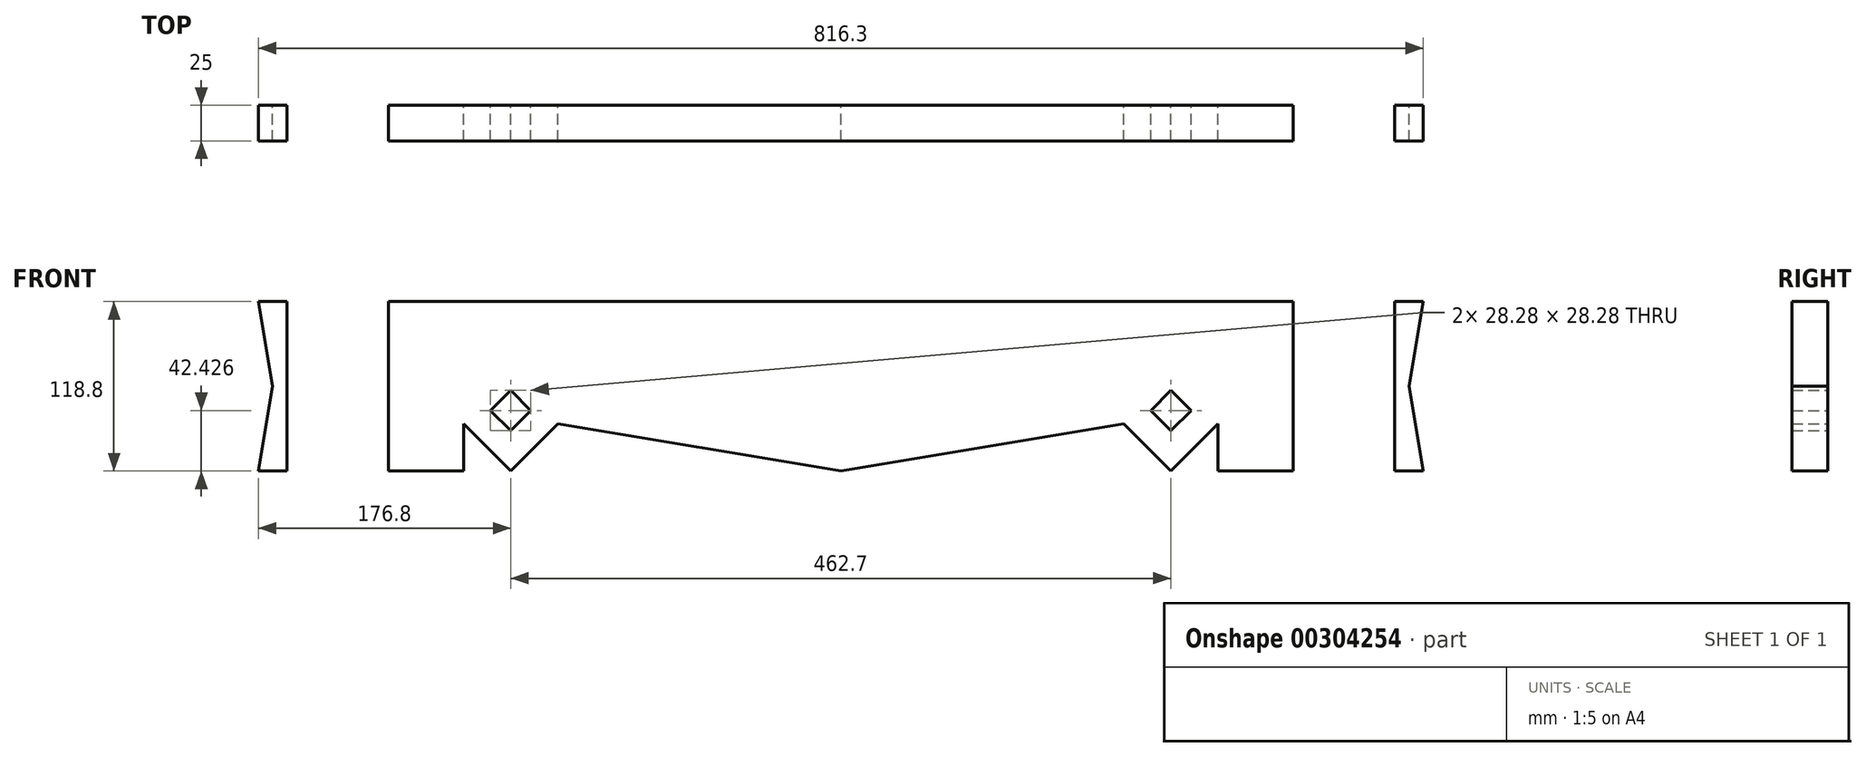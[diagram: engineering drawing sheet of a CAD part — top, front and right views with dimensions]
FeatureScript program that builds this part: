
annotation { "Feature Type Name" : "Feature", "Feature Type Description" : "" }
export const myFeature = defineFeature(function(context is Context, id is Id, definition is map)
    precondition{}
    {
        {
            var Q0;
            Q0=qCreatedBy(makeId("Front.planeOp"),FACE);
            var sketch = newSketch(context, id + "F0", { "sketchPlane" : qUnion([Q0])});
            skLineSegment(sketch, "E0.bottom", {"start": v(408.15, -59.4) * mm, "end": v(-408.15, -59.4) * mm});
            skLineSegment(sketch, "E0.top", {"start": v(408.15, 59.4) * mm, "end": v(-408.15, 59.4) * mm});
            skLineSegment(sketch, "E0.left", {"start": v(408.15, -59.4) * mm, "end": v(408.15, 59.4) * mm});
            skLineSegment(sketch, "E0.right", {"start": v(-408.15, -59.4) * mm, "end": v(-408.15, 59.4) * mm});
            skPoint(sketch, "E0.middle", {"position": v(0, 0) * mm});
            skLineSegment(sketch, "E1", {"start": v(-408.15, 0) * mm, "end": v(408.15, 0) * mm, "construction": true});
            skPoint(sketch, "E2", {"position": v(-398.15, 0) * mm});
            skLineSegment(sketch, "E3", {"start": v(-408.15, 59.4) * mm, "end": v(-398.15, 0) * mm});
            skLineSegment(sketch, "E4", {"start": v(-398.15, 0) * mm, "end": v(-408.15, -59.4) * mm});
            skPoint(sketch, "E5", {"position": v(-388.15, 0) * mm});
            skLineSegment(sketch, "E6", {"start": v(-388.15, 59.4) * mm, "end": v(-388.15, -59.4) * mm});
            skPoint(sketch, "E7", {"position": v(-317.05, 0) * mm});
            skLineSegment(sketch, "E8", {"start": v(-317.05, -59.4) * mm, "end": v(-317.05, 59.4) * mm});
            skPoint(sketch, "E9", {"position": v(-264.35, -59.4) * mm});
            skLineSegment(sketch, "E10", {"start": v(-264.35, -59.4) * mm, "end": v(-264.35, -26.4) * mm});
            skLineSegment(sketch, "E11", {"start": v(-264.35, -26.4) * mm, "end": v(-231.35, -59.4) * mm});
            skLineSegment(sketch, "E12", {"start": v(-231.35, -59.4) * mm, "end": v(-198.35, -26.4) * mm});
            skLineSegment(sketch, "E13", {"start": v(-198.35, -26.4) * mm, "end": v(0, -59.4) * mm});
            skLineSegment(sketch, "E14", {"start": v(-231.35, -59.4) * mm, "end": v(-231.35, 0) * mm, "construction": true});
            skLineSegment(sketch, "E15.bottom", {"start": v(-231.35, -2.83) * mm, "end": v(-217.2, -16.97) * mm});
            skLineSegment(sketch, "E15.top", {"start": v(-245.5, -16.97) * mm, "end": v(-231.35, -31.12) * mm});
            skLineSegment(sketch, "E15.left", {"start": v(-231.35, -2.83) * mm, "end": v(-245.5, -16.97) * mm});
            skLineSegment(sketch, "E15.right", {"start": v(-217.2, -16.97) * mm, "end": v(-231.35, -31.12) * mm});
            skLineSegment(sketch, "E16", {"start": v(-231.35, -2.83) * mm, "end": v(-231.35, -31.12) * mm, "construction": true});
            skLineSegment(sketch, "E17", {"start": v(-245.5, -16.97) * mm, "end": v(-217.2, -16.97) * mm, "construction": true});
            skLineSegment(sketch, "E18", {"start": v(-224.28, -24.04) * mm, "end": v(-210.14, -38.19) * mm, "construction": true});
            skLineSegment(sketch, "E19", {"start": v(-238.42, -24.04) * mm, "end": v(-252.56, -38.19) * mm, "construction": true});
            skLineSegment(sketch, "E20", {"start": v(-388.15, 59.4) * mm, "end": v(-317.05, 59.4) * mm, "construction": true});
            skLineSegment(sketch, "E21", {"start": v(-388.9, 0.04) * mm, "end": v(-317.05, 0) * mm, "construction": true});
            skLineSegment(sketch, "E22", {"start": v(-352.98, 0.02) * mm, "end": v(-352.6, 59.4) * mm, "construction": true});
            skPoint(sketch, "E23", {"position": v(-352.77, 32.12) * mm});
            skCircle(sketch, "E24", {"center": v(-352.77, 32.12) * mm, "radius": 4.25 * mm});
            skCircle(sketch, "E25.MirrorC", {"center": v(-352.8, -32.08) * mm, "radius": 4.25 * mm});
            skLineSegment(sketch, "E26", {"start": v(0, 0) * mm, "end": v(0, -59.4) * mm, "construction": true});
            skLineSegment(sketch, "E27.MirrorCS", {"start": v(217.2, -16.97) * mm, "end": v(231.35, -31.12) * mm});
            skLineSegment(sketch, "E28.MirrorCS", {"start": v(245.5, -16.97) * mm, "end": v(231.35, -31.12) * mm});
            skLineSegment(sketch, "E29.MirrorCS", {"start": v(231.35, -2.83) * mm, "end": v(245.5, -16.97) * mm});
            skLineSegment(sketch, "E30.MirrorCS", {"start": v(231.35, -2.83) * mm, "end": v(217.2, -16.97) * mm});
            skLineSegment(sketch, "E31.MirrorCS", {"start": v(198.35, -26.4) * mm, "end": v(0, -59.4) * mm});
            skLineSegment(sketch, "E32.MirrorCS", {"start": v(231.35, -59.4) * mm, "end": v(198.35, -26.4) * mm});
            skLineSegment(sketch, "E33.MirrorCS", {"start": v(264.35, -26.4) * mm, "end": v(231.35, -59.4) * mm});
            skLineSegment(sketch, "E34.MirrorCS", {"start": v(264.35, -59.4) * mm, "end": v(264.35, -26.4) * mm});
            skCircle(sketch, "E35.MirrorC", {"center": v(352.8, -32.08) * mm, "radius": 4.25 * mm});
            skCircle(sketch, "E36.MirrorC", {"center": v(352.77, 32.12) * mm, "radius": 4.25 * mm});
            skLineSegment(sketch, "E37.MirrorCS", {"start": v(317.05, -59.4) * mm, "end": v(317.05, 59.4) * mm});
            skLineSegment(sketch, "E38.MirrorCS", {"start": v(388.15, 59.4) * mm, "end": v(388.15, -59.4) * mm});
            skLineSegment(sketch, "E39.MirrorCS", {"start": v(408.15, 59.4) * mm, "end": v(398.15, 0) * mm});
            skLineSegment(sketch, "E40.MirrorCS", {"start": v(398.15, 0) * mm, "end": v(408.15, -59.4) * mm});
            skSolve(sketch);
        }
        {
            var Q0;
            {var subQ1=sQuery(id+"F0.wireOp",EDGE,"E3");Q0=makeQuery(id+"F0.imprint","IMPRINT",FACE,{"disambiguationData":[TD([[makeQuery(id+"F0.imprint","IMPRINT",EDGE,{"derivedFrom":subQ1}),1.0]])]});}
            var Q1;
            {var subQ4=sQuery(id+"F0.wireOp",EDGE,"E8");Q1=makeQuery(id+"F0.imprint","IMPRINT",FACE,{"disambiguationData":[TD([[makeQuery(id+"F0.imprint","IMPRINT",EDGE,{"derivedFrom":subQ4}),-1.0]])]});}
            var Q2;
            {var subQ3=sQuery(id+"F0.wireOp",EDGE,"E38.MirrorCS");Q2=makeQuery(id+"F0.imprint","IMPRINT",FACE,{"disambiguationData":[TD([[makeQuery(id+"F0.imprint","IMPRINT",EDGE,{"derivedFrom":subQ3}),1.0]])]});}
            extrude(context, id + "F1", {"entities" : qUnion([Q0, Q1, Q2]), "depth" : 25 * mm});
        }
    });
